# Revit family: FU_Modular_Sandler_Escala_ESC0225TA
name_source: partatom
category: Furniture
units: mm (PartAtom-declared; Revit-internal decimal feet)

## family parameters
Always vertical = Yes
Cut with Voids When Loaded = No
OmniClass Number = 23.40.20.00
OmniClass Title = General Furniture and Specialties
Room Calculation Point = No
Shared = No
Work Plane-Based = No

## types (1)
- Escalas 0225TA
    Default Elevation = 0 mm  [stored 0 ft]
    Depth = 800 mm  [stored 2.62467 ft]
    Description = Upholstered 80cm right seat.
20cm x 80cm x 80cm (measurements without base).
    Manufacturer = Sandler
    Model = Escalas 0225TA
    Seat Elevation = 220 mm  [stored 0.721785 ft]
    Seat Height = 420 mm  [stored 1.37795 ft]
    URL = https://www.sandlerseating.com
    Width = 800 mm  [stored 2.62467 ft]

note: [stored X ft] marks values corroborated as IEEE doubles in the binary element streams (Revit-internal decimal feet)

## geometry (parser evidence)
native form markers: Sweep x3
no freeform markers — native parametric forms only
